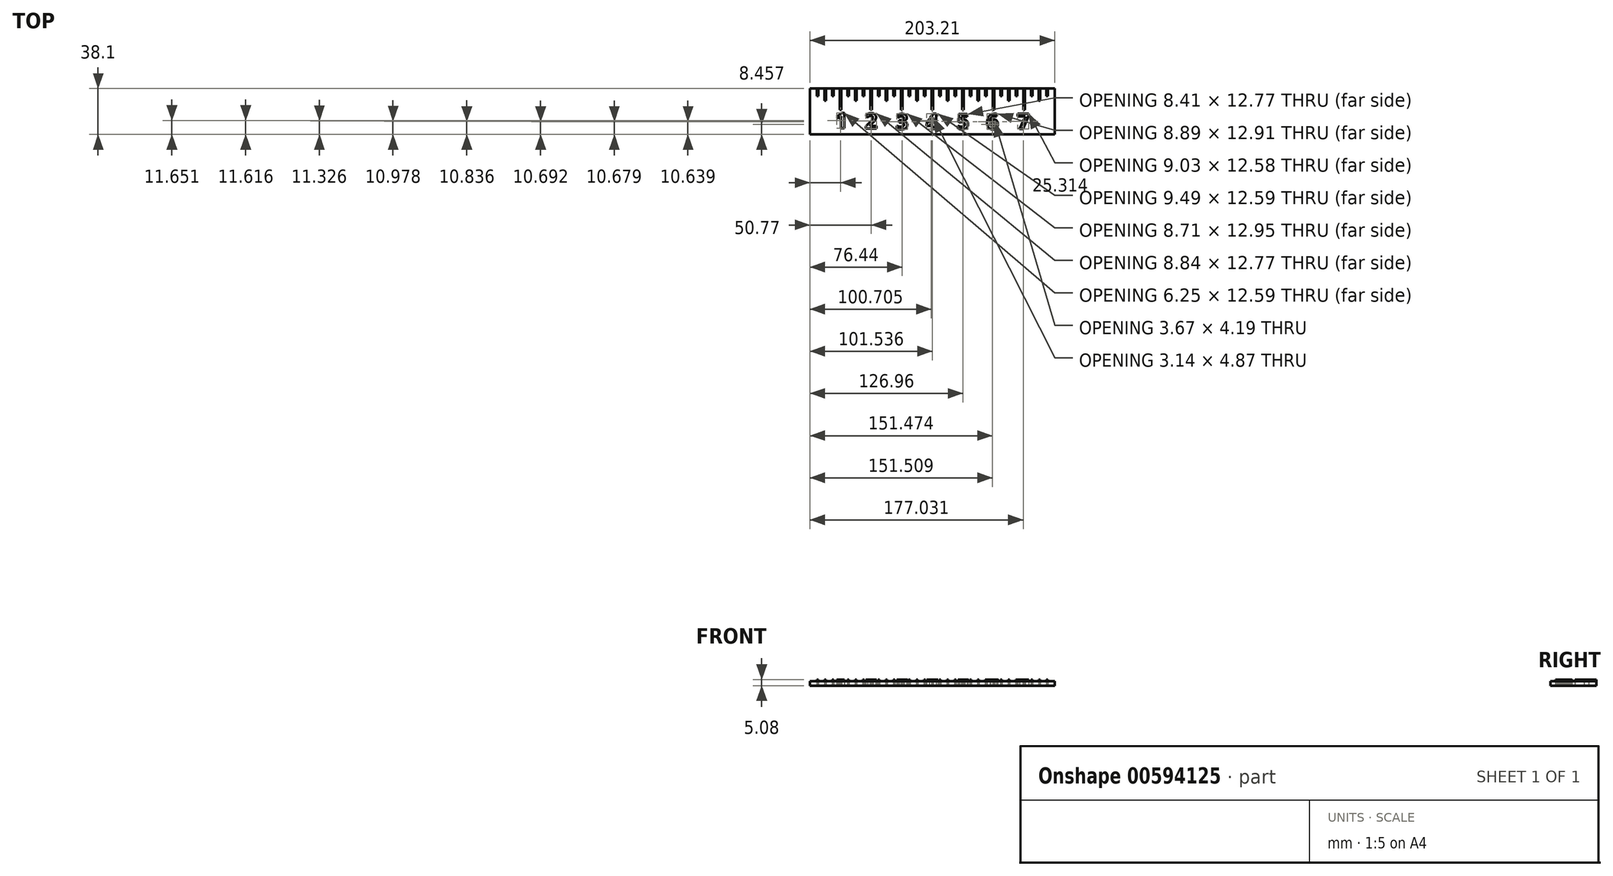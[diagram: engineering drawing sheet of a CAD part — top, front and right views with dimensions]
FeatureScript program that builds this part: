
annotation { "Feature Type Name" : "Feature", "Feature Type Description" : "" }
export const myFeature = defineFeature(function(context is Context, id is Id, definition is map)
    precondition{}
    {
        {
            var Q0;
            Q0=qCreatedBy(makeId("Top.planeOp"),FACE);
            var sketch = newSketch(context, id + "F0", { "sketchPlane" : qUnion([Q0])});
            skLineSegment(sketch, "E0.bottom", {"start": v(-75.57, 29.5) * mm, "end": v(127.64, 29.5) * mm});
            skLineSegment(sketch, "E0.top", {"start": v(-75.56, -8.6) * mm, "end": v(127.64, -8.6) * mm});
            skLineSegment(sketch, "E0.left", {"start": v(-75.57, 29.5) * mm, "end": v(-75.57, -8.6) * mm});
            skLineSegment(sketch, "E0.right", {"start": v(127.64, 29.5) * mm, "end": v(127.64, -8.6) * mm});
            skLineSegment(sketch, "E1", {"start": v(26.04, 29.5) * mm, "end": v(26.04, 11.71) * mm});
            skLineSegment(sketch, "E2", {"start": v(26.04, 29.5) * mm, "end": v(-75.57, 29.5) * mm});
            skLineSegment(sketch, "E3", {"start": v(26.04, 29.5) * mm, "end": v(127.64, 29.5) * mm});
            skLineSegment(sketch, "E4", {"start": v(-24.77, 29.5) * mm, "end": v(-24.77, 11.71) * mm});
            skLineSegment(sketch, "E5", {"start": v(76.84, 29.5) * mm, "end": v(76.84, 11.71) * mm});
            skLineSegment(sketch, "E6", {"start": v(-24.76, 29.5) * mm, "end": v(-75.57, 29.5) * mm});
            skLineSegment(sketch, "E7", {"start": v(-24.76, 29.5) * mm, "end": v(26.04, 29.5) * mm});
            skLineSegment(sketch, "E8", {"start": v(26.04, 29.5) * mm, "end": v(76.83, 29.5) * mm});
            skLineSegment(sketch, "E9", {"start": v(76.83, 29.5) * mm, "end": v(127.64, 29.5) * mm});
            skLineSegment(sketch, "E10", {"start": v(-50.17, 29.5) * mm, "end": v(-50.17, 11.71) * mm});
            skLineSegment(sketch, "E11", {"start": v(0.64, 29.5) * mm, "end": v(0.63, 11.71) * mm});
            skLineSegment(sketch, "E12", {"start": v(51.44, 29.5) * mm, "end": v(51.44, 11.71) * mm});
            skLineSegment(sketch, "E13", {"start": v(102.23, 29.5) * mm, "end": v(102.23, 11.71) * mm});
            skLineSegment(sketch, "E14", {"start": v(-50.17, 11.71) * mm, "end": v(-50.8, 11.71) * mm});
            skLineSegment(sketch, "E15", {"start": v(-50.8, 11.71) * mm, "end": v(-50.8, 29.5) * mm});
            skLineSegment(sketch, "E16", {"start": v(-50.17, 11.71) * mm, "end": v(-49.53, 11.71) * mm});
            skLineSegment(sketch, "E17", {"start": v(-49.53, 11.71) * mm, "end": v(-49.53, 29.5) * mm});
            skLineSegment(sketch, "E18", {"start": v(-24.77, 11.71) * mm, "end": v(-25.4, 11.71) * mm});
            skLineSegment(sketch, "E19", {"start": v(-24.77, 11.71) * mm, "end": v(-24.13, 11.71) * mm});
            skLineSegment(sketch, "E20", {"start": v(-25.4, 11.71) * mm, "end": v(-25.4, 29.5) * mm});
            skLineSegment(sketch, "E21", {"start": v(-24.13, 11.71) * mm, "end": v(-24.13, 29.5) * mm});
            skLineSegment(sketch, "E22", {"start": v(0.63, 11.71) * mm, "end": v(0, 11.71) * mm});
            skLineSegment(sketch, "E23", {"start": v(0, 11.71) * mm, "end": v(0, 29.5) * mm});
            skLineSegment(sketch, "E24", {"start": v(0.63, 11.71) * mm, "end": v(1.27, 11.71) * mm});
            skLineSegment(sketch, "E25", {"start": v(1.27, 11.71) * mm, "end": v(1.27, 29.5) * mm});
            skLineSegment(sketch, "E26", {"start": v(26.04, 11.71) * mm, "end": v(25.4, 11.71) * mm});
            skLineSegment(sketch, "E27", {"start": v(26.04, 11.71) * mm, "end": v(26.67, 11.71) * mm});
            skLineSegment(sketch, "E28", {"start": v(25.4, 11.71) * mm, "end": v(25.4, 29.5) * mm});
            skLineSegment(sketch, "E29", {"start": v(26.67, 11.71) * mm, "end": v(26.67, 29.5) * mm});
            skLineSegment(sketch, "E30", {"start": v(51.44, 11.71) * mm, "end": v(50.8, 11.71) * mm});
            skLineSegment(sketch, "E31", {"start": v(51.44, 11.71) * mm, "end": v(52.07, 11.71) * mm});
            skLineSegment(sketch, "E32", {"start": v(50.8, 11.71) * mm, "end": v(50.8, 29.5) * mm});
            skLineSegment(sketch, "E33", {"start": v(52.07, 11.71) * mm, "end": v(52.07, 29.5) * mm});
            skLineSegment(sketch, "E34", {"start": v(76.84, 11.71) * mm, "end": v(76.2, 11.71) * mm});
            skLineSegment(sketch, "E35", {"start": v(76.84, 11.71) * mm, "end": v(77.47, 11.71) * mm});
            skLineSegment(sketch, "E36", {"start": v(76.2, 11.71) * mm, "end": v(76.2, 29.5) * mm});
            skLineSegment(sketch, "E37", {"start": v(77.47, 11.71) * mm, "end": v(77.47, 29.5) * mm});
            skLineSegment(sketch, "E38", {"start": v(102.23, 11.71) * mm, "end": v(101.6, 11.71) * mm});
            skLineSegment(sketch, "E39", {"start": v(102.23, 11.71) * mm, "end": v(102.87, 11.71) * mm});
            skLineSegment(sketch, "E40", {"start": v(102.87, 11.71) * mm, "end": v(102.87, 29.5) * mm});
            skLineSegment(sketch, "E41", {"start": v(101.6, 11.71) * mm, "end": v(101.6, 29.5) * mm});
            skLineSegment(sketch, "E42", {"start": v(-50.17, 29.5) * mm, "end": v(-24.77, 29.5) * mm});
            skLineSegment(sketch, "E43", {"start": v(-24.76, 29.5) * mm, "end": v(0.64, 29.5) * mm});
            skLineSegment(sketch, "E44", {"start": v(0.64, 29.5) * mm, "end": v(26.04, 29.5) * mm});
            skLineSegment(sketch, "E45", {"start": v(26.04, 29.5) * mm, "end": v(51.44, 29.5) * mm});
            skLineSegment(sketch, "E46", {"start": v(51.44, 29.5) * mm, "end": v(76.84, 29.5) * mm});
            skLineSegment(sketch, "E47", {"start": v(76.83, 29.5) * mm, "end": v(102.23, 29.5) * mm});
            skLineSegment(sketch, "E48", {"start": v(102.23, 29.5) * mm, "end": v(127.64, 29.5) * mm});
            skLineSegment(sketch, "E49", {"start": v(-37.47, 29.5) * mm, "end": v(-37.47, 19.33) * mm});
            skLineSegment(sketch, "E50", {"start": v(-12.06, 29.5) * mm, "end": v(-12.06, 19.33) * mm});
            skLineSegment(sketch, "E51", {"start": v(13.34, 29.5) * mm, "end": v(13.34, 19.33) * mm});
            skLineSegment(sketch, "E52", {"start": v(38.74, 29.5) * mm, "end": v(38.74, 19.33) * mm});
            skLineSegment(sketch, "E53", {"start": v(64.14, 29.5) * mm, "end": v(64.14, 19.33) * mm});
            skLineSegment(sketch, "E54", {"start": v(89.53, 29.5) * mm, "end": v(89.53, 19.33) * mm});
            skLineSegment(sketch, "E55", {"start": v(114.94, 29.5) * mm, "end": v(114.94, 19.33) * mm});
            skLineSegment(sketch, "E56", {"start": v(-50.17, 29.5) * mm, "end": v(-75.57, 29.5) * mm});
            skLineSegment(sketch, "E57", {"start": v(-62.87, 29.5) * mm, "end": v(-62.87, 19.33) * mm});
            skLineSegment(sketch, "E58", {"start": v(-62.87, 19.33) * mm, "end": v(-62.23, 19.33) * mm});
            skLineSegment(sketch, "E59", {"start": v(-62.23, 19.33) * mm, "end": v(-62.87, 19.33) * mm});
            skLineSegment(sketch, "E60", {"start": v(-63.5, 19.33) * mm, "end": v(-62.87, 19.33) * mm});
            skLineSegment(sketch, "E61", {"start": v(-62.23, 19.33) * mm, "end": v(-62.23, 29.5) * mm});
            skLineSegment(sketch, "E62", {"start": v(-63.5, 19.33) * mm, "end": v(-63.5, 29.5) * mm});
            skLineSegment(sketch, "E63", {"start": v(-37.47, 19.33) * mm, "end": v(-36.83, 19.33) * mm});
            skLineSegment(sketch, "E64", {"start": v(-37.47, 19.33) * mm, "end": v(-38.1, 19.33) * mm});
            skLineSegment(sketch, "E65", {"start": v(-38.1, 19.33) * mm, "end": v(-38.1, 29.5) * mm});
            skLineSegment(sketch, "E66", {"start": v(-36.83, 19.33) * mm, "end": v(-36.83, 29.5) * mm});
            skLineSegment(sketch, "E67", {"start": v(-12.06, 19.33) * mm, "end": v(-11.43, 19.33) * mm});
            skLineSegment(sketch, "E68", {"start": v(-12.06, 19.33) * mm, "end": v(-12.7, 19.33) * mm});
            skLineSegment(sketch, "E69", {"start": v(-11.43, 19.33) * mm, "end": v(-11.43, 29.5) * mm});
            skLineSegment(sketch, "E70", {"start": v(-12.7, 19.33) * mm, "end": v(-12.7, 29.5) * mm});
            skLineSegment(sketch, "E71", {"start": v(13.34, 19.33) * mm, "end": v(13.97, 19.33) * mm});
            skLineSegment(sketch, "E72", {"start": v(13.34, 19.33) * mm, "end": v(12.7, 19.33) * mm});
            skLineSegment(sketch, "E73", {"start": v(13.97, 19.33) * mm, "end": v(13.97, 29.5) * mm});
            skLineSegment(sketch, "E74", {"start": v(12.7, 19.33) * mm, "end": v(12.7, 29.5) * mm});
            skLineSegment(sketch, "E75", {"start": v(38.74, 19.33) * mm, "end": v(39.37, 19.33) * mm});
            skLineSegment(sketch, "E76", {"start": v(38.74, 19.33) * mm, "end": v(38.1, 19.33) * mm});
            skLineSegment(sketch, "E77", {"start": v(38.1, 19.33) * mm, "end": v(38.1, 29.5) * mm});
            skLineSegment(sketch, "E78", {"start": v(39.37, 19.33) * mm, "end": v(39.37, 29.5) * mm});
            skLineSegment(sketch, "E79", {"start": v(64.14, 19.33) * mm, "end": v(63.5, 19.33) * mm});
            skLineSegment(sketch, "E80", {"start": v(64.14, 19.33) * mm, "end": v(64.77, 19.33) * mm});
            skLineSegment(sketch, "E81", {"start": v(64.77, 19.33) * mm, "end": v(64.77, 29.5) * mm});
            skLineSegment(sketch, "E82", {"start": v(63.5, 19.33) * mm, "end": v(63.5, 29.5) * mm});
            skLineSegment(sketch, "E83", {"start": v(89.53, 19.33) * mm, "end": v(90.17, 19.33) * mm});
            skLineSegment(sketch, "E84", {"start": v(89.53, 19.33) * mm, "end": v(88.9, 19.33) * mm});
            skLineSegment(sketch, "E85", {"start": v(90.17, 19.33) * mm, "end": v(90.17, 29.5) * mm});
            skLineSegment(sketch, "E86", {"start": v(88.9, 19.33) * mm, "end": v(88.9, 29.5) * mm});
            skLineSegment(sketch, "E87", {"start": v(114.94, 19.33) * mm, "end": v(114.3, 19.33) * mm});
            skLineSegment(sketch, "E88", {"start": v(114.94, 19.33) * mm, "end": v(115.57, 19.33) * mm});
            skLineSegment(sketch, "E89", {"start": v(114.3, 19.33) * mm, "end": v(114.3, 29.5) * mm});
            skLineSegment(sketch, "E90", {"start": v(115.57, 19.33) * mm, "end": v(115.57, 29.5) * mm});
            skLineSegment(sketch, "E91", {"start": v(-75.57, 29.5) * mm, "end": v(-62.87, 29.5) * mm});
            skLineSegment(sketch, "E92", {"start": v(-69.22, 29.5) * mm, "end": v(-69.22, 23.14) * mm});
            skLineSegment(sketch, "E93", {"start": v(-69.22, 23.14) * mm, "end": v(-69.85, 23.14) * mm});
            skLineSegment(sketch, "E94", {"start": v(-69.22, 23.14) * mm, "end": v(-68.58, 23.14) * mm});
            skLineSegment(sketch, "E95", {"start": v(-68.58, 23.14) * mm, "end": v(-68.58, 29.5) * mm});
            skLineSegment(sketch, "E96", {"start": v(-69.85, 23.14) * mm, "end": v(-69.85, 29.5) * mm});
            skLineSegment(sketch, "E97", {"start": v(-62.87, 29.5) * mm, "end": v(-50.17, 29.5) * mm});
            skLineSegment(sketch, "E98", {"start": v(-56.52, 29.5) * mm, "end": v(-56.52, 23.14) * mm});
            skLineSegment(sketch, "E99", {"start": v(-56.52, 23.14) * mm, "end": v(-55.88, 23.14) * mm});
            skLineSegment(sketch, "E100", {"start": v(-56.52, 23.14) * mm, "end": v(-57.15, 23.14) * mm});
            skLineSegment(sketch, "E101", {"start": v(-55.88, 23.14) * mm, "end": v(-55.88, 29.5) * mm});
            skLineSegment(sketch, "E102", {"start": v(-57.15, 23.14) * mm, "end": v(-57.15, 29.5) * mm});
            skLineSegment(sketch, "E103", {"start": v(-50.17, 29.5) * mm, "end": v(-37.47, 29.5) * mm});
            skLineSegment(sketch, "E104", {"start": v(-43.82, 29.5) * mm, "end": v(-43.82, 23.14) * mm});
            skLineSegment(sketch, "E105", {"start": v(-43.82, 23.14) * mm, "end": v(-44.45, 23.14) * mm});
            skLineSegment(sketch, "E106", {"start": v(-43.82, 23.14) * mm, "end": v(-43.18, 23.14) * mm});
            skLineSegment(sketch, "E107", {"start": v(-44.45, 23.14) * mm, "end": v(-44.45, 29.5) * mm});
            skLineSegment(sketch, "E108", {"start": v(-43.18, 23.14) * mm, "end": v(-43.18, 29.5) * mm});
            skLineSegment(sketch, "E109", {"start": v(-37.47, 29.5) * mm, "end": v(-24.77, 29.5) * mm});
            skLineSegment(sketch, "E110", {"start": v(-31.12, 29.5) * mm, "end": v(-31.12, 23.14) * mm});
            skLineSegment(sketch, "E111", {"start": v(-31.12, 23.14) * mm, "end": v(-31.75, 23.14) * mm});
            skLineSegment(sketch, "E112", {"start": v(-31.12, 23.14) * mm, "end": v(-30.48, 23.14) * mm});
            skLineSegment(sketch, "E113", {"start": v(-31.75, 23.14) * mm, "end": v(-31.75, 29.5) * mm});
            skLineSegment(sketch, "E114", {"start": v(-30.48, 23.14) * mm, "end": v(-30.48, 29.5) * mm});
            skLineSegment(sketch, "E115", {"start": v(-24.77, 29.5) * mm, "end": v(-12.06, 29.5) * mm});
            skLineSegment(sketch, "E116", {"start": v(-18.41, 29.5) * mm, "end": v(-18.41, 23.14) * mm});
            skLineSegment(sketch, "E117", {"start": v(-18.41, 23.14) * mm, "end": v(-17.78, 23.14) * mm});
            skLineSegment(sketch, "E118", {"start": v(-18.41, 23.14) * mm, "end": v(-19.05, 23.14) * mm});
            skLineSegment(sketch, "E119", {"start": v(-19.05, 23.14) * mm, "end": v(-19.05, 29.5) * mm});
            skLineSegment(sketch, "E120", {"start": v(-17.78, 23.14) * mm, "end": v(-17.78, 29.5) * mm});
            skLineSegment(sketch, "E121", {"start": v(0.64, 29.5) * mm, "end": v(-12.06, 29.5) * mm});
            skLineSegment(sketch, "E122", {"start": v(-5.71, 29.5) * mm, "end": v(-5.71, 23.14) * mm});
            skLineSegment(sketch, "E123", {"start": v(-5.71, 23.14) * mm, "end": v(-6.35, 23.14) * mm});
            skLineSegment(sketch, "E124", {"start": v(-5.71, 23.14) * mm, "end": v(-5.08, 23.14) * mm});
            skLineSegment(sketch, "E125", {"start": v(-6.35, 23.14) * mm, "end": v(-6.35, 29.5) * mm});
            skLineSegment(sketch, "E126", {"start": v(-5.08, 23.14) * mm, "end": v(-5.08, 29.5) * mm});
            skLineSegment(sketch, "E127", {"start": v(0.64, 29.5) * mm, "end": v(13.34, 29.5) * mm});
            skLineSegment(sketch, "E128", {"start": v(6.99, 29.5) * mm, "end": v(6.99, 23.14) * mm});
            skLineSegment(sketch, "E129", {"start": v(6.99, 23.14) * mm, "end": v(6.35, 23.14) * mm});
            skLineSegment(sketch, "E130", {"start": v(6.99, 23.14) * mm, "end": v(7.62, 23.14) * mm});
            skLineSegment(sketch, "E131", {"start": v(6.35, 23.14) * mm, "end": v(6.35, 29.5) * mm});
            skLineSegment(sketch, "E132", {"start": v(7.62, 23.14) * mm, "end": v(7.62, 29.5) * mm});
            skLineSegment(sketch, "E133", {"start": v(13.34, 29.5) * mm, "end": v(26.04, 29.5) * mm});
            skLineSegment(sketch, "E134", {"start": v(19.69, 29.5) * mm, "end": v(19.69, 23.14) * mm});
            skLineSegment(sketch, "E135", {"start": v(19.69, 23.14) * mm, "end": v(20.32, 23.14) * mm});
            skLineSegment(sketch, "E136", {"start": v(19.69, 23.14) * mm, "end": v(19.05, 23.14) * mm});
            skLineSegment(sketch, "E137", {"start": v(19.05, 23.14) * mm, "end": v(19.05, 29.5) * mm});
            skLineSegment(sketch, "E138", {"start": v(20.32, 23.14) * mm, "end": v(20.32, 29.5) * mm});
            skLineSegment(sketch, "E139", {"start": v(26.04, 29.5) * mm, "end": v(38.74, 29.5) * mm});
            skLineSegment(sketch, "E140", {"start": v(32.39, 29.5) * mm, "end": v(32.39, 23.14) * mm});
            skLineSegment(sketch, "E141", {"start": v(32.39, 23.14) * mm, "end": v(31.75, 23.14) * mm});
            skLineSegment(sketch, "E142", {"start": v(32.39, 23.14) * mm, "end": v(33.02, 23.14) * mm});
            skLineSegment(sketch, "E143", {"start": v(31.75, 23.14) * mm, "end": v(31.75, 29.5) * mm});
            skLineSegment(sketch, "E144", {"start": v(33.02, 23.14) * mm, "end": v(33.02, 29.5) * mm});
            skLineSegment(sketch, "E145", {"start": v(38.74, 29.5) * mm, "end": v(51.44, 29.5) * mm});
            skLineSegment(sketch, "E146", {"start": v(45.09, 29.5) * mm, "end": v(45.09, 23.14) * mm});
            skLineSegment(sketch, "E147", {"start": v(45.09, 23.14) * mm, "end": v(45.72, 23.14) * mm});
            skLineSegment(sketch, "E148", {"start": v(45.09, 23.14) * mm, "end": v(44.45, 23.14) * mm});
            skLineSegment(sketch, "E149", {"start": v(44.45, 23.14) * mm, "end": v(44.45, 29.5) * mm});
            skLineSegment(sketch, "E150", {"start": v(45.72, 23.14) * mm, "end": v(45.72, 29.5) * mm});
            skLineSegment(sketch, "E151", {"start": v(51.44, 29.5) * mm, "end": v(64.14, 29.5) * mm});
            skLineSegment(sketch, "E152", {"start": v(57.79, 29.5) * mm, "end": v(57.79, 23.14) * mm});
            skLineSegment(sketch, "E153", {"start": v(57.79, 23.14) * mm, "end": v(58.42, 23.14) * mm});
            skLineSegment(sketch, "E154", {"start": v(57.79, 23.14) * mm, "end": v(57.15, 23.14) * mm});
            skLineSegment(sketch, "E155", {"start": v(58.42, 23.14) * mm, "end": v(58.42, 29.5) * mm});
            skLineSegment(sketch, "E156", {"start": v(57.15, 23.14) * mm, "end": v(57.15, 29.5) * mm});
            skLineSegment(sketch, "E157", {"start": v(64.14, 29.5) * mm, "end": v(76.84, 29.5) * mm});
            skLineSegment(sketch, "E158", {"start": v(70.49, 29.5) * mm, "end": v(70.49, 23.14) * mm});
            skLineSegment(sketch, "E159", {"start": v(70.49, 23.14) * mm, "end": v(71.12, 23.14) * mm});
            skLineSegment(sketch, "E160", {"start": v(70.49, 23.14) * mm, "end": v(69.85, 23.14) * mm});
            skLineSegment(sketch, "E161", {"start": v(71.12, 23.14) * mm, "end": v(71.12, 29.5) * mm});
            skLineSegment(sketch, "E162", {"start": v(69.85, 23.14) * mm, "end": v(69.85, 29.5) * mm});
            skLineSegment(sketch, "E163", {"start": v(76.84, 29.5) * mm, "end": v(89.53, 29.5) * mm});
            skLineSegment(sketch, "E164", {"start": v(83.19, 29.5) * mm, "end": v(83.19, 23.14) * mm});
            skLineSegment(sketch, "E165", {"start": v(83.19, 23.14) * mm, "end": v(82.55, 23.14) * mm});
            skLineSegment(sketch, "E166", {"start": v(82.55, 23.14) * mm, "end": v(82.55, 29.5) * mm});
            skLineSegment(sketch, "E167", {"start": v(83.19, 23.14) * mm, "end": v(83.82, 23.14) * mm});
            skLineSegment(sketch, "E168", {"start": v(83.82, 23.14) * mm, "end": v(83.82, 29.5) * mm});
            skLineSegment(sketch, "E169", {"start": v(89.53, 29.5) * mm, "end": v(102.23, 29.5) * mm});
            skLineSegment(sketch, "E170", {"start": v(95.88, 29.5) * mm, "end": v(95.88, 23.14) * mm});
            skLineSegment(sketch, "E171", {"start": v(95.88, 23.14) * mm, "end": v(96.52, 23.14) * mm});
            skLineSegment(sketch, "E172", {"start": v(95.88, 23.14) * mm, "end": v(95.25, 23.14) * mm});
            skLineSegment(sketch, "E173", {"start": v(95.25, 23.14) * mm, "end": v(95.25, 29.5) * mm});
            skLineSegment(sketch, "E174", {"start": v(96.52, 23.14) * mm, "end": v(96.52, 29.5) * mm});
            skLineSegment(sketch, "E175", {"start": v(102.23, 29.5) * mm, "end": v(114.94, 29.5) * mm});
            skLineSegment(sketch, "E176", {"start": v(108.59, 29.5) * mm, "end": v(108.59, 23.14) * mm});
            skLineSegment(sketch, "E177", {"start": v(108.59, 23.14) * mm, "end": v(109.22, 23.14) * mm});
            skLineSegment(sketch, "E178", {"start": v(108.59, 23.14) * mm, "end": v(107.95, 23.14) * mm});
            skLineSegment(sketch, "E179", {"start": v(109.22, 23.14) * mm, "end": v(109.22, 29.5) * mm});
            skLineSegment(sketch, "E180", {"start": v(107.95, 23.14) * mm, "end": v(107.95, 29.5) * mm});
            skLineSegment(sketch, "E181", {"start": v(114.94, 29.5) * mm, "end": v(127.64, 29.5) * mm});
            skLineSegment(sketch, "E182", {"start": v(121.29, 29.5) * mm, "end": v(121.29, 23.14) * mm});
            skLineSegment(sketch, "E183", {"start": v(121.29, 23.14) * mm, "end": v(121.92, 23.14) * mm});
            skLineSegment(sketch, "E184", {"start": v(121.29, 23.14) * mm, "end": v(120.65, 23.14) * mm});
            skLineSegment(sketch, "E185", {"start": v(121.92, 23.14) * mm, "end": v(121.92, 29.5) * mm});
            skLineSegment(sketch, "E186", {"start": v(120.65, 23.14) * mm, "end": v(120.65, 29.5) * mm});
            skText(sketch, "E187", { "text": "1", "fontName": "OpenSans-Bold.ttf"});
            skText(sketch, "E188", { "text": "2\n", "fontName": "OpenSans-Bold.ttf"});
            skText(sketch, "E189", { "text": "3", "fontName": "OpenSans-Bold.ttf"});
            skText(sketch, "E190", { "text": "4", "fontName": "OpenSans-Bold.ttf"});
            skText(sketch, "E191", { "text": "5\n", "fontName": "OpenSans-Bold.ttf"});
            skText(sketch, "E192", { "text": "6", "fontName": "OpenSans-Bold.ttf"});
            skText(sketch, "E193", { "text": "7", "fontName": "OpenSans-Bold.ttf"});
            const initialGuessF0  = {"E187": [-0.05442, -0.00329, 1, 0, 0.0127], "E188": [-0.02989, -0.00367, 1, 0, 0.0127], "E189": [-0.00416, -0.00423, 1, 0, 0.0127], "E190": [0.02092, -0.00407, 1, 0, 0.0127], "E191": [0.04632, -0.00418, 1, 0, 0.0127], "E192": [0.07084, -0.0042, 1, 0, 0.0127], "E193": [0.09647, -0.00392, 1, 0, 0.0127]};
            skSetInitialGuess(sketch, initialGuessF0);
            skSolve(sketch);
        }
        {
            var Q0;
            Q0=makeQuery(id+"F0.imprint","IMPRINT",FACE,{"disambiguationData":[TD([[makeQuery(id+"F0.imprint","IMPRINT",EDGE,{"derivedFrom":sQuery(id+"F0.wireOp",EDGE,"E0.top")}),1.0]])]});
            var Q1;
            Q1=makeQuery(id+"F0.imprint","IMPRINT",FACE,{"disambiguationData":[TD([[makeQuery(id+"F0.imprint","IMPRINT",EDGE,{"derivedFrom":sQuery(id+"F0.wireOp",EDGE,"E190.sketch_text.stroke-11")}),1.0]])]});
            var Q2;
            Q2=makeQuery(id+"F0.imprint","IMPRINT",FACE,{"disambiguationData":[TD([[makeQuery(id+"F0.imprint","IMPRINT",EDGE,{"derivedFrom":sQuery(id+"F0.wireOp",EDGE,"E192.sketch_text.stroke-17")}),1.0]])]});
            extrude(context, id + "F1", {"entities" : qUnion([Q0, Q1, Q2]), "depth" : 3.8 * mm, "offsetDistance" : 25.4 * mm});
        }
        {
            var Q0;
            {var subQ0=sQuery(id+"F0.wireOp",EDGE,"E92");Q0=makeQuery(id+"F0.imprint","IMPRINT",FACE,{"disambiguationData":[TD([[makeQuery(id+"F0.imprint","IMPRINT",EDGE,{"derivedFrom":subQ0}),1.0]])]});}
            var Q1;
            {var subQ0=sQuery(id+"F0.wireOp",EDGE,"E92");Q1=makeQuery(id+"F0.imprint","IMPRINT",FACE,{"disambiguationData":[TD([[makeQuery(id+"F0.imprint","IMPRINT",EDGE,{"derivedFrom":subQ0}),-1.0]])]});}
            var Q2;
            {var subQ0=sQuery(id+"F0.wireOp",EDGE,"E57");Q2=makeQuery(id+"F0.imprint","IMPRINT",FACE,{"disambiguationData":[TD([[makeQuery(id+"F0.imprint","IMPRINT",EDGE,{"derivedFrom":subQ0}),-1.0]])]});}
            var Q3;
            {var subQ0=sQuery(id+"F0.wireOp",EDGE,"E57");Q3=makeQuery(id+"F0.imprint","IMPRINT",FACE,{"disambiguationData":[TD([[makeQuery(id+"F0.imprint","IMPRINT",EDGE,{"derivedFrom":subQ0}),1.0]])]});}
            var Q4;
            {var subQ0=sQuery(id+"F0.wireOp",EDGE,"E98");Q4=makeQuery(id+"F0.imprint","IMPRINT",FACE,{"disambiguationData":[TD([[makeQuery(id+"F0.imprint","IMPRINT",EDGE,{"derivedFrom":subQ0}),-1.0]])]});}
            var Q5;
            {var subQ0=sQuery(id+"F0.wireOp",EDGE,"E98");Q5=makeQuery(id+"F0.imprint","IMPRINT",FACE,{"disambiguationData":[TD([[makeQuery(id+"F0.imprint","IMPRINT",EDGE,{"derivedFrom":subQ0}),1.0]])]});}
            var Q6;
            {var subQ0=sQuery(id+"F0.wireOp",EDGE,"E10");Q6=makeQuery(id+"F0.imprint","IMPRINT",FACE,{"disambiguationData":[TD([[makeQuery(id+"F0.imprint","IMPRINT",EDGE,{"derivedFrom":subQ0}),-1.0]])]});}
            var Q7;
            {var subQ0=sQuery(id+"F0.wireOp",EDGE,"E10");Q7=makeQuery(id+"F0.imprint","IMPRINT",FACE,{"disambiguationData":[TD([[makeQuery(id+"F0.imprint","IMPRINT",EDGE,{"derivedFrom":subQ0}),1.0]])]});}
            var Q8;
            {var subQ0=sQuery(id+"F0.wireOp",EDGE,"E104");Q8=makeQuery(id+"F0.imprint","IMPRINT",FACE,{"disambiguationData":[TD([[makeQuery(id+"F0.imprint","IMPRINT",EDGE,{"derivedFrom":subQ0}),-1.0]])]});}
            var Q9;
            {var subQ0=sQuery(id+"F0.wireOp",EDGE,"E49");Q9=makeQuery(id+"F0.imprint","IMPRINT",FACE,{"disambiguationData":[TD([[makeQuery(id+"F0.imprint","IMPRINT",EDGE,{"derivedFrom":subQ0}),1.0]])]});}
            var Q10;
            {var subQ0=sQuery(id+"F0.wireOp",EDGE,"E110");Q10=makeQuery(id+"F0.imprint","IMPRINT",FACE,{"disambiguationData":[TD([[makeQuery(id+"F0.imprint","IMPRINT",EDGE,{"derivedFrom":subQ0}),-1.0]])]});}
            var Q11;
            {var subQ0=sQuery(id+"F0.wireOp",EDGE,"E110");Q11=makeQuery(id+"F0.imprint","IMPRINT",FACE,{"disambiguationData":[TD([[makeQuery(id+"F0.imprint","IMPRINT",EDGE,{"derivedFrom":subQ0}),1.0]])]});}
            var Q12;
            {var subQ0=sQuery(id+"F0.wireOp",EDGE,"E104");Q12=makeQuery(id+"F0.imprint","IMPRINT",FACE,{"disambiguationData":[TD([[makeQuery(id+"F0.imprint","IMPRINT",EDGE,{"derivedFrom":subQ0}),1.0]])]});}
            var Q13;
            {var subQ0=sQuery(id+"F0.wireOp",EDGE,"E49");Q13=makeQuery(id+"F0.imprint","IMPRINT",FACE,{"disambiguationData":[TD([[makeQuery(id+"F0.imprint","IMPRINT",EDGE,{"derivedFrom":subQ0}),-1.0]])]});}
            var Q14;
            {var subQ0=sQuery(id+"F0.wireOp",EDGE,"E4");Q14=makeQuery(id+"F0.imprint","IMPRINT",FACE,{"disambiguationData":[TD([[makeQuery(id+"F0.imprint","IMPRINT",EDGE,{"derivedFrom":subQ0}),-1.0]])]});}
            var Q15;
            {var subQ0=sQuery(id+"F0.wireOp",EDGE,"E4");Q15=makeQuery(id+"F0.imprint","IMPRINT",FACE,{"disambiguationData":[TD([[makeQuery(id+"F0.imprint","IMPRINT",EDGE,{"derivedFrom":subQ0}),1.0]])]});}
            var Q16;
            {var subQ0=sQuery(id+"F0.wireOp",EDGE,"E116");Q16=makeQuery(id+"F0.imprint","IMPRINT",FACE,{"disambiguationData":[TD([[makeQuery(id+"F0.imprint","IMPRINT",EDGE,{"derivedFrom":subQ0}),-1.0]])]});}
            var Q17;
            {var subQ0=sQuery(id+"F0.wireOp",EDGE,"E116");Q17=makeQuery(id+"F0.imprint","IMPRINT",FACE,{"disambiguationData":[TD([[makeQuery(id+"F0.imprint","IMPRINT",EDGE,{"derivedFrom":subQ0}),1.0]])]});}
            var Q18;
            {var subQ0=sQuery(id+"F0.wireOp",EDGE,"E50");Q18=makeQuery(id+"F0.imprint","IMPRINT",FACE,{"disambiguationData":[TD([[makeQuery(id+"F0.imprint","IMPRINT",EDGE,{"derivedFrom":subQ0}),1.0]])]});}
            var Q19;
            {var subQ0=sQuery(id+"F0.wireOp",EDGE,"E122");Q19=makeQuery(id+"F0.imprint","IMPRINT",FACE,{"disambiguationData":[TD([[makeQuery(id+"F0.imprint","IMPRINT",EDGE,{"derivedFrom":subQ0}),-1.0]])]});}
            var Q20;
            {var subQ0=sQuery(id+"F0.wireOp",EDGE,"E50");Q20=makeQuery(id+"F0.imprint","IMPRINT",FACE,{"disambiguationData":[TD([[makeQuery(id+"F0.imprint","IMPRINT",EDGE,{"derivedFrom":subQ0}),-1.0]])]});}
            var Q21;
            {var subQ0=sQuery(id+"F0.wireOp",EDGE,"E122");Q21=makeQuery(id+"F0.imprint","IMPRINT",FACE,{"disambiguationData":[TD([[makeQuery(id+"F0.imprint","IMPRINT",EDGE,{"derivedFrom":subQ0}),1.0]])]});}
            var Q22;
            {var subQ0=sQuery(id+"F0.wireOp",EDGE,"E11");Q22=makeQuery(id+"F0.imprint","IMPRINT",FACE,{"disambiguationData":[TD([[makeQuery(id+"F0.imprint","IMPRINT",EDGE,{"derivedFrom":subQ0}),-1.0]])]});}
            var Q23;
            {var subQ0=sQuery(id+"F0.wireOp",EDGE,"E11");Q23=makeQuery(id+"F0.imprint","IMPRINT",FACE,{"disambiguationData":[TD([[makeQuery(id+"F0.imprint","IMPRINT",EDGE,{"derivedFrom":subQ0}),1.0]])]});}
            var Q24;
            {var subQ0=sQuery(id+"F0.wireOp",EDGE,"E128");Q24=makeQuery(id+"F0.imprint","IMPRINT",FACE,{"disambiguationData":[TD([[makeQuery(id+"F0.imprint","IMPRINT",EDGE,{"derivedFrom":subQ0}),-1.0]])]});}
            var Q25;
            {var subQ0=sQuery(id+"F0.wireOp",EDGE,"E128");Q25=makeQuery(id+"F0.imprint","IMPRINT",FACE,{"disambiguationData":[TD([[makeQuery(id+"F0.imprint","IMPRINT",EDGE,{"derivedFrom":subQ0}),1.0]])]});}
            var Q26;
            {var subQ0=sQuery(id+"F0.wireOp",EDGE,"E51");Q26=makeQuery(id+"F0.imprint","IMPRINT",FACE,{"disambiguationData":[TD([[makeQuery(id+"F0.imprint","IMPRINT",EDGE,{"derivedFrom":subQ0}),-1.0]])]});}
            var Q27;
            {var subQ0=sQuery(id+"F0.wireOp",EDGE,"E51");Q27=makeQuery(id+"F0.imprint","IMPRINT",FACE,{"disambiguationData":[TD([[makeQuery(id+"F0.imprint","IMPRINT",EDGE,{"derivedFrom":subQ0}),1.0]])]});}
            var Q28;
            {var subQ0=sQuery(id+"F0.wireOp",EDGE,"E134");Q28=makeQuery(id+"F0.imprint","IMPRINT",FACE,{"disambiguationData":[TD([[makeQuery(id+"F0.imprint","IMPRINT",EDGE,{"derivedFrom":subQ0}),1.0]])]});}
            var Q29;
            {var subQ0=sQuery(id+"F0.wireOp",EDGE,"E134");Q29=makeQuery(id+"F0.imprint","IMPRINT",FACE,{"disambiguationData":[TD([[makeQuery(id+"F0.imprint","IMPRINT",EDGE,{"derivedFrom":subQ0}),-1.0]])]});}
            var Q30;
            {var subQ0=sQuery(id+"F0.wireOp",EDGE,"E1");Q30=makeQuery(id+"F0.imprint","IMPRINT",FACE,{"disambiguationData":[TD([[makeQuery(id+"F0.imprint","IMPRINT",EDGE,{"derivedFrom":subQ0}),1.0]])]});}
            var Q31;
            {var subQ0=sQuery(id+"F0.wireOp",EDGE,"E1");Q31=makeQuery(id+"F0.imprint","IMPRINT",FACE,{"disambiguationData":[TD([[makeQuery(id+"F0.imprint","IMPRINT",EDGE,{"derivedFrom":subQ0}),-1.0]])]});}
            var Q32;
            {var subQ0=sQuery(id+"F0.wireOp",EDGE,"E140");Q32=makeQuery(id+"F0.imprint","IMPRINT",FACE,{"disambiguationData":[TD([[makeQuery(id+"F0.imprint","IMPRINT",EDGE,{"derivedFrom":subQ0}),-1.0]])]});}
            var Q33;
            {var subQ0=sQuery(id+"F0.wireOp",EDGE,"E140");Q33=makeQuery(id+"F0.imprint","IMPRINT",FACE,{"disambiguationData":[TD([[makeQuery(id+"F0.imprint","IMPRINT",EDGE,{"derivedFrom":subQ0}),1.0]])]});}
            var Q34;
            {var subQ0=sQuery(id+"F0.wireOp",EDGE,"E52");Q34=makeQuery(id+"F0.imprint","IMPRINT",FACE,{"disambiguationData":[TD([[makeQuery(id+"F0.imprint","IMPRINT",EDGE,{"derivedFrom":subQ0}),-1.0]])]});}
            var Q35;
            {var subQ0=sQuery(id+"F0.wireOp",EDGE,"E52");Q35=makeQuery(id+"F0.imprint","IMPRINT",FACE,{"disambiguationData":[TD([[makeQuery(id+"F0.imprint","IMPRINT",EDGE,{"derivedFrom":subQ0}),1.0]])]});}
            var Q36;
            {var subQ0=sQuery(id+"F0.wireOp",EDGE,"E146");Q36=makeQuery(id+"F0.imprint","IMPRINT",FACE,{"disambiguationData":[TD([[makeQuery(id+"F0.imprint","IMPRINT",EDGE,{"derivedFrom":subQ0}),-1.0]])]});}
            var Q37;
            {var subQ0=sQuery(id+"F0.wireOp",EDGE,"E146");Q37=makeQuery(id+"F0.imprint","IMPRINT",FACE,{"disambiguationData":[TD([[makeQuery(id+"F0.imprint","IMPRINT",EDGE,{"derivedFrom":subQ0}),1.0]])]});}
            var Q38;
            {var subQ0=sQuery(id+"F0.wireOp",EDGE,"E12");Q38=makeQuery(id+"F0.imprint","IMPRINT",FACE,{"disambiguationData":[TD([[makeQuery(id+"F0.imprint","IMPRINT",EDGE,{"derivedFrom":subQ0}),-1.0]])]});}
            var Q39;
            {var subQ0=sQuery(id+"F0.wireOp",EDGE,"E12");Q39=makeQuery(id+"F0.imprint","IMPRINT",FACE,{"disambiguationData":[TD([[makeQuery(id+"F0.imprint","IMPRINT",EDGE,{"derivedFrom":subQ0}),1.0]])]});}
            var Q40;
            {var subQ0=sQuery(id+"F0.wireOp",EDGE,"E152");Q40=makeQuery(id+"F0.imprint","IMPRINT",FACE,{"disambiguationData":[TD([[makeQuery(id+"F0.imprint","IMPRINT",EDGE,{"derivedFrom":subQ0}),-1.0]])]});}
            var Q41;
            {var subQ0=sQuery(id+"F0.wireOp",EDGE,"E53");Q41=makeQuery(id+"F0.imprint","IMPRINT",FACE,{"disambiguationData":[TD([[makeQuery(id+"F0.imprint","IMPRINT",EDGE,{"derivedFrom":subQ0}),-1.0]])]});}
            var Q42;
            {var subQ0=sQuery(id+"F0.wireOp",EDGE,"E152");Q42=makeQuery(id+"F0.imprint","IMPRINT",FACE,{"disambiguationData":[TD([[makeQuery(id+"F0.imprint","IMPRINT",EDGE,{"derivedFrom":subQ0}),1.0]])]});}
            var Q43;
            {var subQ0=sQuery(id+"F0.wireOp",EDGE,"E53");Q43=makeQuery(id+"F0.imprint","IMPRINT",FACE,{"disambiguationData":[TD([[makeQuery(id+"F0.imprint","IMPRINT",EDGE,{"derivedFrom":subQ0}),1.0]])]});}
            var Q44;
            {var subQ0=sQuery(id+"F0.wireOp",EDGE,"E158");Q44=makeQuery(id+"F0.imprint","IMPRINT",FACE,{"disambiguationData":[TD([[makeQuery(id+"F0.imprint","IMPRINT",EDGE,{"derivedFrom":subQ0}),-1.0]])]});}
            var Q45;
            {var subQ0=sQuery(id+"F0.wireOp",EDGE,"E158");Q45=makeQuery(id+"F0.imprint","IMPRINT",FACE,{"disambiguationData":[TD([[makeQuery(id+"F0.imprint","IMPRINT",EDGE,{"derivedFrom":subQ0}),1.0]])]});}
            var Q46;
            {var subQ0=sQuery(id+"F0.wireOp",EDGE,"E5");Q46=makeQuery(id+"F0.imprint","IMPRINT",FACE,{"disambiguationData":[TD([[makeQuery(id+"F0.imprint","IMPRINT",EDGE,{"derivedFrom":subQ0}),-1.0]])]});}
            var Q47;
            {var subQ0=sQuery(id+"F0.wireOp",EDGE,"E5");Q47=makeQuery(id+"F0.imprint","IMPRINT",FACE,{"disambiguationData":[TD([[makeQuery(id+"F0.imprint","IMPRINT",EDGE,{"derivedFrom":subQ0}),1.0]])]});}
            var Q48;
            {var subQ0=sQuery(id+"F0.wireOp",EDGE,"E164");Q48=makeQuery(id+"F0.imprint","IMPRINT",FACE,{"disambiguationData":[TD([[makeQuery(id+"F0.imprint","IMPRINT",EDGE,{"derivedFrom":subQ0}),-1.0]])]});}
            var Q49;
            {var subQ0=sQuery(id+"F0.wireOp",EDGE,"E164");Q49=makeQuery(id+"F0.imprint","IMPRINT",FACE,{"disambiguationData":[TD([[makeQuery(id+"F0.imprint","IMPRINT",EDGE,{"derivedFrom":subQ0}),1.0]])]});}
            var Q50;
            {var subQ0=sQuery(id+"F0.wireOp",EDGE,"E54");Q50=makeQuery(id+"F0.imprint","IMPRINT",FACE,{"disambiguationData":[TD([[makeQuery(id+"F0.imprint","IMPRINT",EDGE,{"derivedFrom":subQ0}),-1.0]])]});}
            var Q51;
            {var subQ0=sQuery(id+"F0.wireOp",EDGE,"E54");Q51=makeQuery(id+"F0.imprint","IMPRINT",FACE,{"disambiguationData":[TD([[makeQuery(id+"F0.imprint","IMPRINT",EDGE,{"derivedFrom":subQ0}),1.0]])]});}
            var Q52;
            {var subQ0=sQuery(id+"F0.wireOp",EDGE,"E170");Q52=makeQuery(id+"F0.imprint","IMPRINT",FACE,{"disambiguationData":[TD([[makeQuery(id+"F0.imprint","IMPRINT",EDGE,{"derivedFrom":subQ0}),-1.0]])]});}
            var Q53;
            {var subQ0=sQuery(id+"F0.wireOp",EDGE,"E170");Q53=makeQuery(id+"F0.imprint","IMPRINT",FACE,{"disambiguationData":[TD([[makeQuery(id+"F0.imprint","IMPRINT",EDGE,{"derivedFrom":subQ0}),1.0]])]});}
            var Q54;
            {var subQ0=sQuery(id+"F0.wireOp",EDGE,"E13");Q54=makeQuery(id+"F0.imprint","IMPRINT",FACE,{"disambiguationData":[TD([[makeQuery(id+"F0.imprint","IMPRINT",EDGE,{"derivedFrom":subQ0}),-1.0]])]});}
            var Q55;
            {var subQ0=sQuery(id+"F0.wireOp",EDGE,"E13");Q55=makeQuery(id+"F0.imprint","IMPRINT",FACE,{"disambiguationData":[TD([[makeQuery(id+"F0.imprint","IMPRINT",EDGE,{"derivedFrom":subQ0}),1.0]])]});}
            var Q56;
            {var subQ0=sQuery(id+"F0.wireOp",EDGE,"E176");Q56=makeQuery(id+"F0.imprint","IMPRINT",FACE,{"disambiguationData":[TD([[makeQuery(id+"F0.imprint","IMPRINT",EDGE,{"derivedFrom":subQ0}),-1.0]])]});}
            var Q57;
            {var subQ0=sQuery(id+"F0.wireOp",EDGE,"E176");Q57=makeQuery(id+"F0.imprint","IMPRINT",FACE,{"disambiguationData":[TD([[makeQuery(id+"F0.imprint","IMPRINT",EDGE,{"derivedFrom":subQ0}),1.0]])]});}
            var Q58;
            {var subQ0=sQuery(id+"F0.wireOp",EDGE,"E55");Q58=makeQuery(id+"F0.imprint","IMPRINT",FACE,{"disambiguationData":[TD([[makeQuery(id+"F0.imprint","IMPRINT",EDGE,{"derivedFrom":subQ0}),-1.0]])]});}
            var Q59;
            {var subQ0=sQuery(id+"F0.wireOp",EDGE,"E55");Q59=makeQuery(id+"F0.imprint","IMPRINT",FACE,{"disambiguationData":[TD([[makeQuery(id+"F0.imprint","IMPRINT",EDGE,{"derivedFrom":subQ0}),1.0]])]});}
            var Q60;
            {var subQ0=sQuery(id+"F0.wireOp",EDGE,"E182");Q60=makeQuery(id+"F0.imprint","IMPRINT",FACE,{"disambiguationData":[TD([[makeQuery(id+"F0.imprint","IMPRINT",EDGE,{"derivedFrom":subQ0}),-1.0]])]});}
            var Q61;
            {var subQ0=sQuery(id+"F0.wireOp",EDGE,"E182");Q61=makeQuery(id+"F0.imprint","IMPRINT",FACE,{"disambiguationData":[TD([[makeQuery(id+"F0.imprint","IMPRINT",EDGE,{"derivedFrom":subQ0}),1.0]])]});}
            var Q62;
            Q62=makeQuery(id+"F0.imprint","IMPRINT",FACE,{"disambiguationData":[TD([[makeQuery(id+"F0.imprint","IMPRINT",EDGE,{"derivedFrom":sQuery(id+"F0.wireOp",EDGE,"E188.sketch_text.stroke-0")}),-1.0]])]});
            var Q63;
            Q63=makeQuery(id+"F0.imprint","IMPRINT",FACE,{"disambiguationData":[TD([[makeQuery(id+"F0.imprint","IMPRINT",EDGE,{"derivedFrom":sQuery(id+"F0.wireOp",EDGE,"E187.sketch_text.stroke-0")}),-1.0]])]});
            var Q64;
            Q64=makeQuery(id+"F0.imprint","IMPRINT",FACE,{"disambiguationData":[TD([[makeQuery(id+"F0.imprint","IMPRINT",EDGE,{"derivedFrom":sQuery(id+"F0.wireOp",EDGE,"E189.sketch_text.stroke-0")}),-1.0]])]});
            var Q65;
            Q65=makeQuery(id+"F0.imprint","IMPRINT",FACE,{"disambiguationData":[TD([[makeQuery(id+"F0.imprint","IMPRINT",EDGE,{"derivedFrom":sQuery(id+"F0.wireOp",EDGE,"E190.sketch_text.stroke-0")}),-1.0]])]});
            var Q66;
            Q66=makeQuery(id+"F0.imprint","IMPRINT",FACE,{"disambiguationData":[TD([[makeQuery(id+"F0.imprint","IMPRINT",EDGE,{"derivedFrom":sQuery(id+"F0.wireOp",EDGE,"E191.sketch_text.stroke-0")}),-1.0]])]});
            var Q67;
            Q67=makeQuery(id+"F0.imprint","IMPRINT",FACE,{"disambiguationData":[TD([[makeQuery(id+"F0.imprint","IMPRINT",EDGE,{"derivedFrom":sQuery(id+"F0.wireOp",EDGE,"E192.sketch_text.stroke-0")}),-1.0]])]});
            var Q68;
            Q68=makeQuery(id+"F0.imprint","IMPRINT",FACE,{"disambiguationData":[TD([[makeQuery(id+"F0.imprint","IMPRINT",EDGE,{"derivedFrom":sQuery(id+"F0.wireOp",EDGE,"E193.sketch_text.stroke-0")}),-1.0]])]});
            extrude(context, id + "F2", {"entities" : qUnion([Q0, Q1, Q2, Q3, Q4, Q5, Q6, Q7, Q8, Q9, Q10, Q11, Q12, Q13, Q14, Q15, Q16, Q17, Q18, Q19, Q20, Q21, Q22, Q23, Q24, Q25, Q26, Q27, Q28, Q29, Q30, Q31, Q32, Q33, Q34, Q35, Q36, Q37, Q38, Q39, Q40, Q41, Q42, Q43, Q44, Q45, Q46, Q47, Q48, Q49, Q50, Q51, Q52, Q53, Q54, Q55, Q56, Q57, Q58, Q59, Q60, Q61, Q62, Q63, Q64, Q65, Q66, Q67, Q68]), "depth" : 5.08 * mm, "offsetDistance" : 25.4 * mm});
        }
    });
